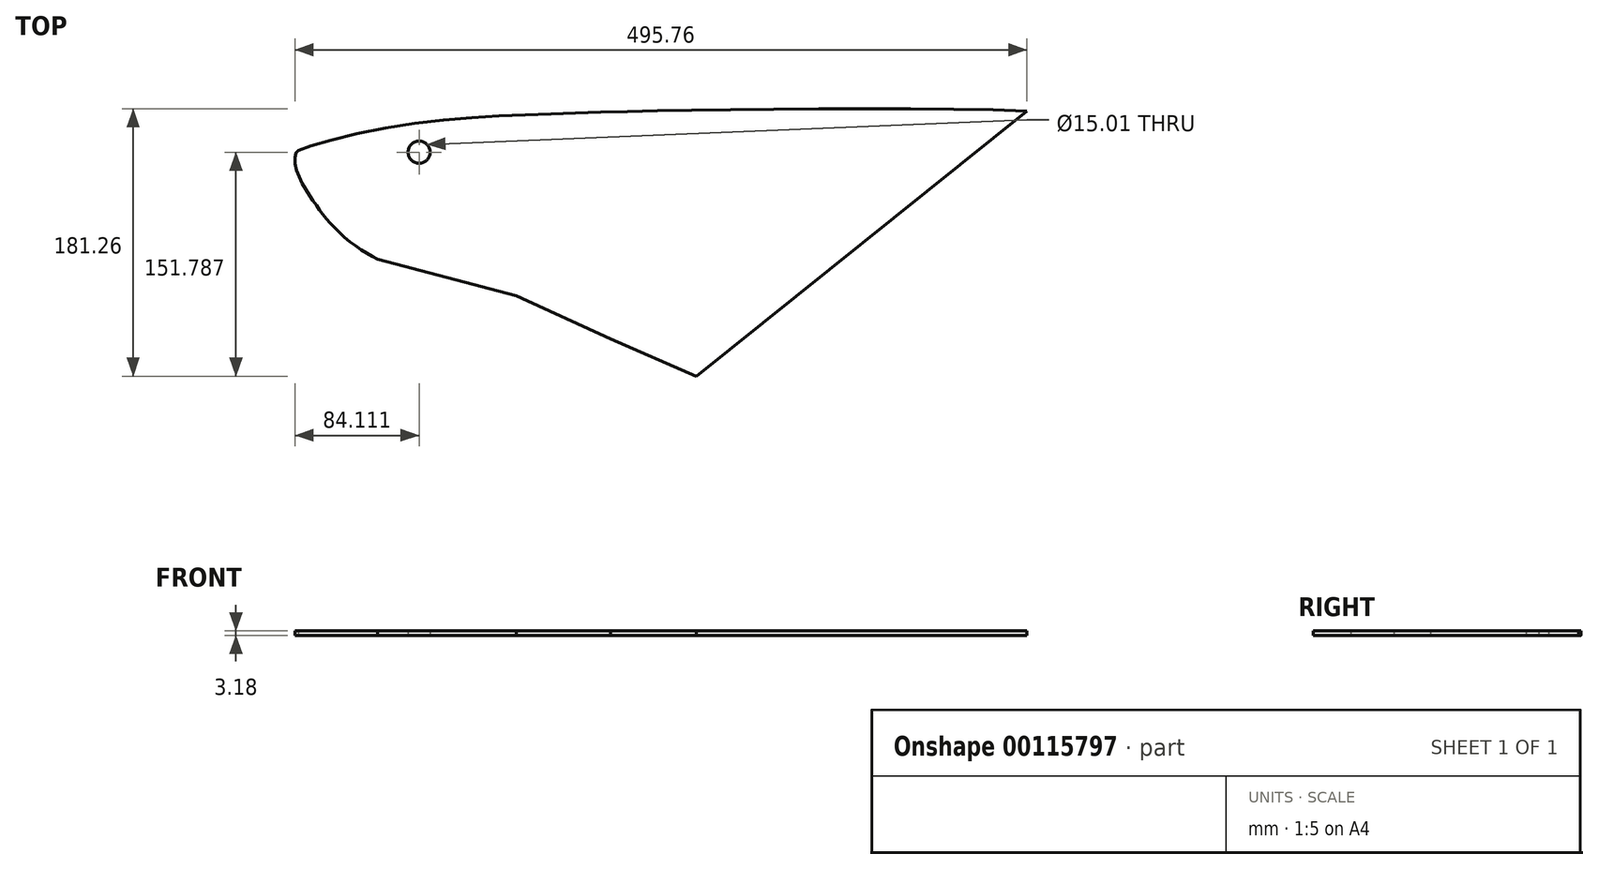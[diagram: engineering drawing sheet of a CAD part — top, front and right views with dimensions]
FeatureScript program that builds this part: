
annotation { "Feature Type Name" : "Feature", "Feature Type Description" : "" }
export const myFeature = defineFeature(function(context is Context, id is Id, definition is map)
    precondition{}
    {
        {
            var Q0;
            Q0=qCreatedBy(makeId("Top.planeOp"),FACE);
            var sketch = newSketch(context, id + "F0", { "sketchPlane" : qUnion([Q0])});
            skFitSpline(sketch, "E0", {"points": [v(195.87, 197.86) * mm, v(-31.05, 198.47) * mm, v(-131.93, 195.61) * mm, v(-230.35, 187.7) * mm, v(-297.68, 171.02) * mm], "startDerivative": vector(-478.9, 18.66) * mm, "endDerivative": vector(-126.28, -62.2) * mm});
            skFitSpline(sketch, "E1", {"points": [v(-297.68, 171.02) * mm, v(-299.18, 159.42) * mm, v(-288.03, 137.66) * mm, v(-278.37, 124.5) * mm, v(-262.57, 109.13) * mm, v(-243.94, 97.42) * mm], "startDerivative": vector(-45.62, -13.28) * mm, "endDerivative": vector(80.31, -41.34) * mm});
            skLineSegment(sketch, "E2", {"start": v(-243.94, 97.42) * mm, "end": v(-150.07, 72.78) * mm});
            skLineSegment(sketch, "E3", {"start": v(-150.07, 72.78) * mm, "end": v(-86.1, 43.6) * mm});
            skLineSegment(sketch, "E4", {"start": v(-27.91, 18.13) * mm, "end": v(-86.1, 43.6) * mm});
            skLineSegment(sketch, "E5", {"start": v(195.87, 197.86) * mm, "end": v(-27.91, 18.13) * mm});
            skCircle(sketch, "E6", {"center": v(-215.78, 169.92) * mm, "radius": 7.5 * mm});
            skSolve(sketch);
        }
        {
            var Q0;
            Q0=makeQuery(id+"F0.imprint","IMPRINT",FACE,{"disambiguationData":[TD([[makeQuery(id+"F0.imprint","IMPRINT",EDGE,{"derivedFrom":sQuery(id+"F0.wireOp",EDGE,"E0")}),1.0]])]});
            extrude(context, id + "F1", {"entities" : qUnion([Q0]), "depth" : 3.17 * mm});
        }
    });
